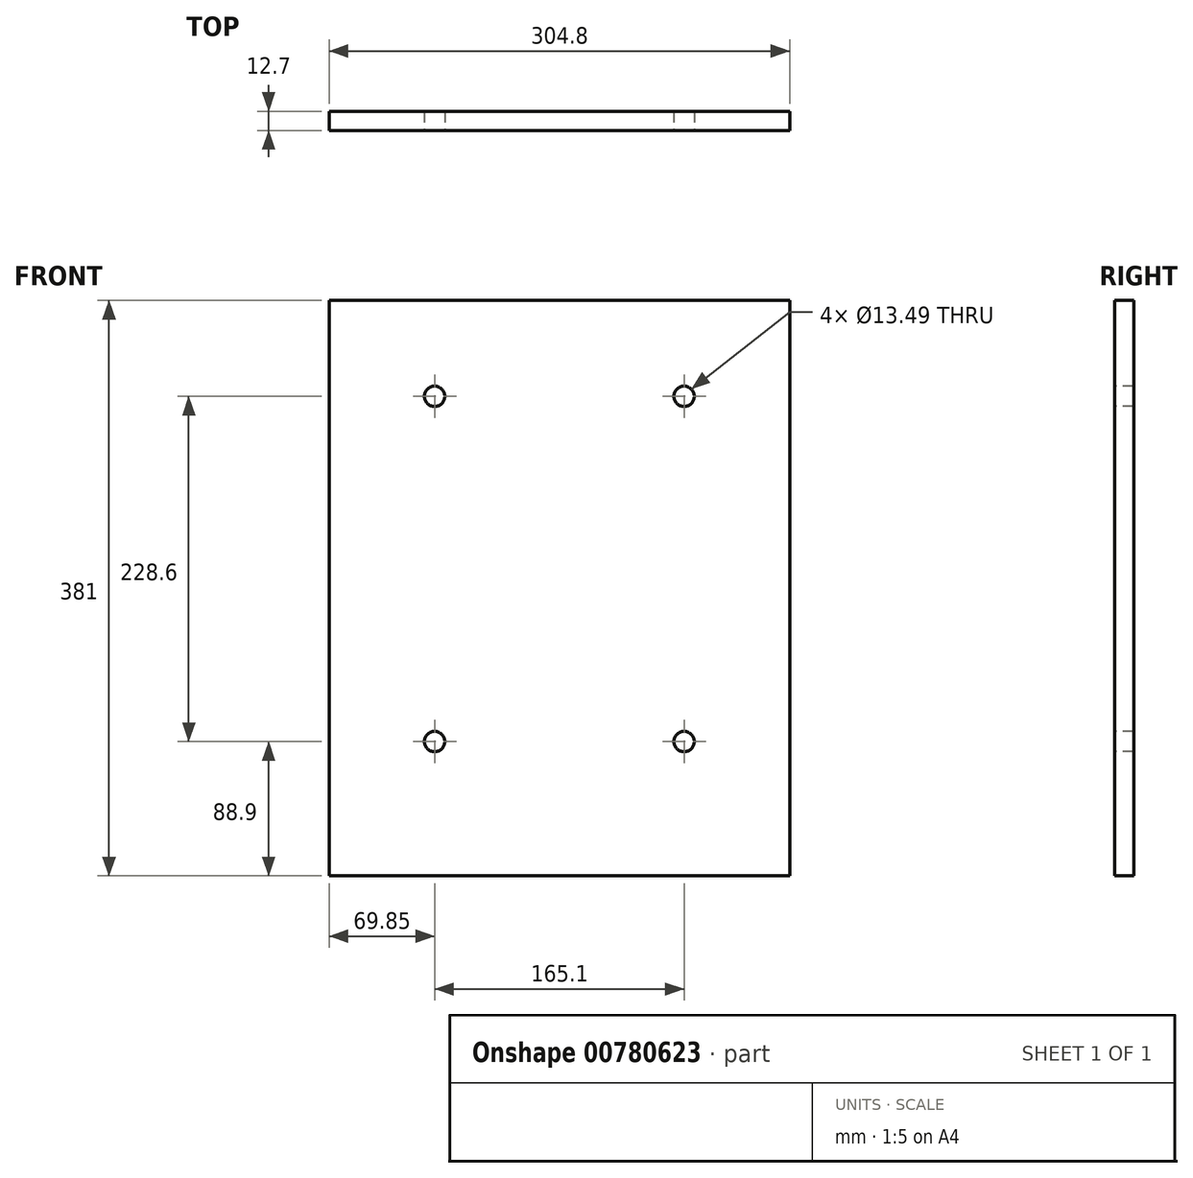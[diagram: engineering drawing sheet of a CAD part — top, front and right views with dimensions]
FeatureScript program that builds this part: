
annotation { "Feature Type Name" : "Feature", "Feature Type Description" : "" }
export const myFeature = defineFeature(function(context is Context, id is Id, definition is map)
    precondition{}
    {
        {
            var Q0;
            Q0=qCreatedBy(makeId("Front.planeOp"),FACE);
            var sketch = newSketch(context, id + "F0", { "sketchPlane" : qUnion([Q0])});
            skLineSegment(sketch, "E0.bottom", {"start": v(0, 0) * mm, "end": v(304.8, 0) * mm});
            skLineSegment(sketch, "E0.top", {"start": v(0, 381) * mm, "end": v(304.8, 381) * mm});
            skLineSegment(sketch, "E0.left", {"start": v(0, 0) * mm, "end": v(0, 381) * mm});
            skLineSegment(sketch, "E0.right", {"start": v(304.8, 0) * mm, "end": v(304.8, 381) * mm});
            skSolve(sketch);
        }
        {
            var Q0;
            Q0=makeQuery(id+"F0.imprint","IMPRINT",FACE,{"disambiguationData":[TD([[makeQuery(id+"F0.imprint","IMPRINT",EDGE,{"derivedFrom":sQuery(id+"F0.wireOp",EDGE,"E0.bottom")}),1.0]])]});
            extrude(context, id + "F1", {"entities" : qUnion([Q0]), "depth" : 12.7 * mm, "offsetDistance" : 25.4 * mm});
        }
        {
            var Q0;
            Q0=makeQuery(id+"F1.opExtrude","CAP_FACE",FACE,{"disambiguationData":[OSD([sQuery(id+"F0.wireOp",EDGE,"E0.bottom"),sQuery(id+"F0.wireOp",EDGE,"E0.top"),sQuery(id+"F0.wireOp",EDGE,"E0.left"),sQuery(id+"F0.wireOp",EDGE,"E0.right")])],"isStart":false});
            var sketch = newSketch(context, id + "F2", { "sketchPlane" : qUnion([Q0])});
            skPoint(sketch, "E1", {"position": v(69.85, 317.5) * mm});
            skPoint(sketch, "E2", {"position": v(234.95, 317.5) * mm});
            skPoint(sketch, "E3", {"position": v(69.85, 88.9) * mm});
            skPoint(sketch, "E4", {"position": v(234.95, 88.9) * mm});
            skSolve(sketch);
        }
        {
            var Q0;
            Q0=sQuery(id+"F2.wireOp",VERTEX,"E1");
            var Q1;
            Q1=sQuery(id+"F2.wireOp",VERTEX,"E2");
            var Q2;
            Q2=sQuery(id+"F2.wireOp",VERTEX,"E3");
            var Q3;
            Q3=sQuery(id+"F2.wireOp",VERTEX,"E4");
            var Q4;
            Q4=makeQuery(id+"F1.opExtrude","SWEPT_BODY",BODY,{"disambiguationData":[OSD([sQuery(id+"F0.wireOp",EDGE,"E0.bottom"),sQuery(id+"F0.wireOp",EDGE,"E0.top"),sQuery(id+"F0.wireOp",EDGE,"E0.left"),sQuery(id+"F0.wireOp",EDGE,"E0.right")])]});
            hole(context, id + "F3", {"style" : HoleStyle.SIMPLE, "endStyle" : HoleEndStyle.THROUGH, "standardTappedOrClearance" : lookupTablePath({ "standard" : "ANSI", "fit" : "Normal (ASME)", "size" : "1/2", "type" : "Clearance" }), "standardBlindInLast" : lookupTablePath({ "fit" : "Free", "standard" : "ANSI", "size" : "1/2", "type" : "Clearance" }), "holeDiameter" : 13.5 * mm, "majorDiameter" : 6.35 * mm, "isTappedThrough" : true, "tappedDepth" : 25.4 * mm, "tapClearance" : 3, "locations" : qUnion([Q0, Q1, Q2, Q3]), "scope" : qUnion([Q4])});
        }
    });
